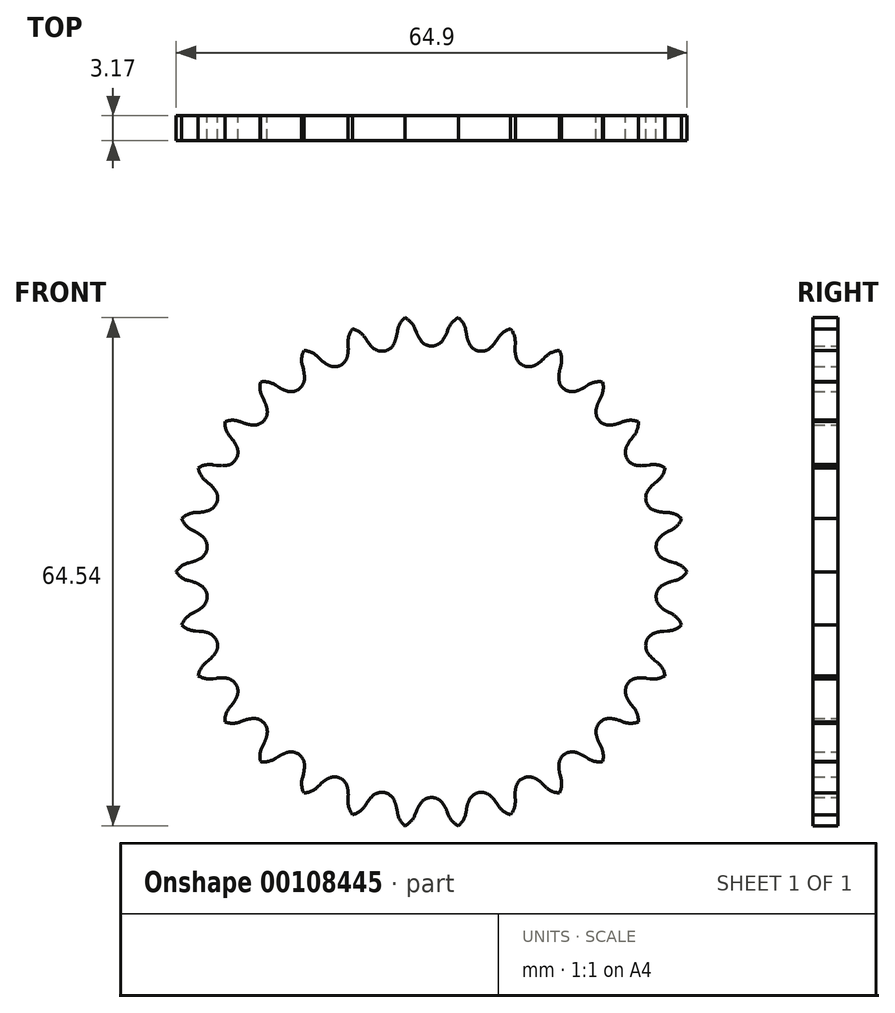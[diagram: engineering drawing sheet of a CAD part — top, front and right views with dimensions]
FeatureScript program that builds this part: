
annotation { "Feature Type Name" : "Feature", "Feature Type Description" : "" }
export const myFeature = defineFeature(function(context is Context, id is Id, definition is map)
    precondition{}
    {
        {
            var Q0;
            Q0=qCreatedBy(makeId("Front.planeOp"),FACE);
            var sketch = newSketch(context, id + "F0", { "sketchPlane" : qUnion([Q0])});
            skCircle(sketch, "E0", {"center": v(0, 0) * mm, "radius": 30.37 * mm, "construction": true});
            skArc(sketch, "E1", {"start": v(-1.36, 29.35) * mm, "mid": v(-0.76, 28.86) * mm, "end": v(0, 28.68) * mm});
            skArc(sketch, "E2", {"start": v(-1.36, 29.35) * mm, "mid": v(-1.69, 29.86) * mm, "end": v(-1.94, 30.42) * mm});
            skLineSegment(sketch, "E3", {"start": v(-1.94, 30.42) * mm, "end": v(-2.1, 30.84) * mm});
            skArc(sketch, "E4.trimOffspring", {"start": v(-2.1, 30.84) * mm, "mid": v(-2.62, 31.68) * mm, "end": v(-3.4, 32.27) * mm});
            skArc(sketch, "E5.MirrorCS", {"start": v(1.36, 29.35) * mm, "mid": v(0.76, 28.86) * mm, "end": v(0, 28.68) * mm});
            skArc(sketch, "E6.MirrorCS", {"start": v(1.36, 29.35) * mm, "mid": v(1.69, 29.86) * mm, "end": v(1.94, 30.42) * mm});
            skLineSegment(sketch, "E7.MirrorCS", {"start": v(1.94, 30.42) * mm, "end": v(2.1, 30.84) * mm});
            skArc(sketch, "E8.MirrorCS", {"start": v(2.1, 30.84) * mm, "mid": v(2.62, 31.68) * mm, "end": v(3.4, 32.27) * mm});
            skArc(sketch, "E9.1.0", {"start": v(-8.47, 29.73) * mm, "mid": v(-9.14, 30.44) * mm, "end": v(-10.03, 30.86) * mm});
            skArc(sketch, "E9.1.1", {"start": v(-7.43, 28.43) * mm, "mid": v(-6.74, 28.07) * mm, "end": v(-5.96, 28.05) * mm});
            skArc(sketch, "E9.1.2", {"start": v(-4.78, 29) * mm, "mid": v(-5.26, 28.38) * mm, "end": v(-5.96, 28.05) * mm});
            skArc(sketch, "E9.1.3", {"start": v(-4.35, 30.6) * mm, "mid": v(-4.03, 31.53) * mm, "end": v(-3.4, 32.27) * mm});
            skArc(sketch, "E9.1.4", {"start": v(-4.78, 29) * mm, "mid": v(-4.56, 29.56) * mm, "end": v(-4.42, 30.16) * mm});
            skLineSegment(sketch, "E9.1.5", {"start": v(-4.42, 30.16) * mm, "end": v(-4.35, 30.6) * mm});
            skArc(sketch, "E9.1.6", {"start": v(-7.43, 28.43) * mm, "mid": v(-7.86, 28.86) * mm, "end": v(-8.22, 29.35) * mm});
            skLineSegment(sketch, "E9.1.7", {"start": v(-8.22, 29.35) * mm, "end": v(-8.47, 29.73) * mm});
            skArc(sketch, "E9.2.0", {"start": v(-14.47, 27.32) * mm, "mid": v(-15.27, 27.87) * mm, "end": v(-16.22, 28.1) * mm});
            skArc(sketch, "E9.2.1", {"start": v(-13.18, 26.26) * mm, "mid": v(-12.43, 26.05) * mm, "end": v(-11.66, 26.2) * mm});
            skArc(sketch, "E9.2.2", {"start": v(-10.7, 27.37) * mm, "mid": v(-11.05, 26.67) * mm, "end": v(-11.66, 26.2) * mm});
            skArc(sketch, "E9.2.3", {"start": v(-10.62, 29.03) * mm, "mid": v(-10.5, 30) * mm, "end": v(-10.03, 30.86) * mm});
            skArc(sketch, "E9.2.4", {"start": v(-10.7, 27.37) * mm, "mid": v(-10.6, 27.97) * mm, "end": v(-10.6, 28.58) * mm});
            skLineSegment(sketch, "E9.2.5", {"start": v(-10.6, 28.58) * mm, "end": v(-10.62, 29.03) * mm});
            skArc(sketch, "E9.2.6", {"start": v(-13.18, 26.26) * mm, "mid": v(-13.69, 26.6) * mm, "end": v(-14.15, 27) * mm});
            skLineSegment(sketch, "E9.2.7", {"start": v(-14.15, 27) * mm, "end": v(-14.47, 27.32) * mm});
            skArc(sketch, "E10.1.3.0", {"start": v(-19.83, 23.71) * mm, "mid": v(-20.74, 24.09) * mm, "end": v(-21.71, 24.11) * mm});
            skArc(sketch, "E10.4.3.0", {"start": v(-18.35, 22.95) * mm, "mid": v(-17.57, 22.9) * mm, "end": v(-16.86, 23.2) * mm});
            skArc(sketch, "E10.8.3.0", {"start": v(-16.16, 24.54) * mm, "mid": v(-16.35, 23.8) * mm, "end": v(-16.86, 23.2) * mm});
            skArc(sketch, "E10.12.3.0", {"start": v(-16.43, 26.2) * mm, "mid": v(-16.5, 27.16) * mm, "end": v(-16.22, 28.1) * mm});
            skArc(sketch, "E10.16.3.0", {"start": v(-16.16, 24.54) * mm, "mid": v(-16.19, 25.15) * mm, "end": v(-16.3, 25.75) * mm});
            skLineSegment(sketch, "E10.20.3.0", {"start": v(-16.3, 25.75) * mm, "end": v(-16.43, 26.2) * mm});
            skArc(sketch, "E10.23.3.0", {"start": v(-18.35, 22.95) * mm, "mid": v(-18.92, 23.17) * mm, "end": v(-19.45, 23.47) * mm});
            skLineSegment(sketch, "E10.27.3.0", {"start": v(-19.45, 23.47) * mm, "end": v(-19.83, 23.71) * mm});
            skArc(sketch, "E10.1.4.0", {"start": v(-24.33, 19.07) * mm, "mid": v(-25.3, 19.25) * mm, "end": v(-26.25, 19.07) * mm});
            skArc(sketch, "E10.4.4.0", {"start": v(-22.72, 18.63) * mm, "mid": v(-21.95, 18.75) * mm, "end": v(-21.31, 19.19) * mm});
            skArc(sketch, "E10.8.4.0", {"start": v(-20.9, 20.65) * mm, "mid": v(-20.94, 19.87) * mm, "end": v(-21.31, 19.19) * mm});
            skArc(sketch, "E10.12.4.0", {"start": v(-21.51, 22.2) * mm, "mid": v(-21.8, 23.14) * mm, "end": v(-21.71, 24.11) * mm});
            skArc(sketch, "E10.16.4.0", {"start": v(-20.9, 20.65) * mm, "mid": v(-21.07, 21.24) * mm, "end": v(-21.3, 21.8) * mm});
            skLineSegment(sketch, "E10.20.4.0", {"start": v(-21.3, 21.8) * mm, "end": v(-21.51, 22.2) * mm});
            skArc(sketch, "E10.23.4.0", {"start": v(-22.72, 18.63) * mm, "mid": v(-23.32, 18.73) * mm, "end": v(-23.9, 18.9) * mm});
            skLineSegment(sketch, "E10.27.4.0", {"start": v(-23.9, 18.9) * mm, "end": v(-24.33, 19.07) * mm});
            skArc(sketch, "E10.1.5.0", {"start": v(-27.76, 13.6) * mm, "mid": v(-28.74, 13.57) * mm, "end": v(-29.64, 13.2) * mm});
            skArc(sketch, "E10.4.5.0", {"start": v(-26.1, 13.5) * mm, "mid": v(-25.37, 13.77) * mm, "end": v(-24.84, 14.34) * mm});
            skArc(sketch, "E10.8.5.0", {"start": v(-24.74, 15.85) * mm, "mid": v(-24.61, 15.08) * mm, "end": v(-24.84, 14.34) * mm});
            skArc(sketch, "E10.12.5.0", {"start": v(-25.66, 17.25) * mm, "mid": v(-26.12, 18.1) * mm, "end": v(-26.25, 19.07) * mm});
            skArc(sketch, "E10.16.5.0", {"start": v(-24.74, 15.85) * mm, "mid": v(-25.02, 16.4) * mm, "end": v(-25.37, 16.9) * mm});
            skLineSegment(sketch, "E10.20.5.0", {"start": v(-25.37, 16.9) * mm, "end": v(-25.66, 17.25) * mm});
            skArc(sketch, "E10.23.5.0", {"start": v(-26.1, 13.5) * mm, "mid": v(-26.7, 13.47) * mm, "end": v(-27.31, 13.53) * mm});
            skLineSegment(sketch, "E10.27.5.0", {"start": v(-27.31, 13.53) * mm, "end": v(-27.76, 13.6) * mm});
            skArc(sketch, "E10.1.6.0", {"start": v(-29.98, 7.53) * mm, "mid": v(-30.93, 7.3) * mm, "end": v(-31.74, 6.75) * mm});
            skArc(sketch, "E10.4.6.0", {"start": v(-28.34, 7.78) * mm, "mid": v(-27.68, 8.2) * mm, "end": v(-27.27, 8.86) * mm});
            skArc(sketch, "E10.8.6.0", {"start": v(-27.5, 10.36) * mm, "mid": v(-27.2, 9.64) * mm, "end": v(-27.27, 8.86) * mm});
            skArc(sketch, "E10.12.6.0", {"start": v(-28.68, 11.53) * mm, "mid": v(-29.32, 12.28) * mm, "end": v(-29.64, 13.2) * mm});
            skArc(sketch, "E10.16.6.0", {"start": v(-27.5, 10.36) * mm, "mid": v(-27.88, 10.83) * mm, "end": v(-28.33, 11.25) * mm});
            skLineSegment(sketch, "E10.20.6.0", {"start": v(-28.33, 11.25) * mm, "end": v(-28.68, 11.53) * mm});
            skArc(sketch, "E10.23.6.0", {"start": v(-28.34, 7.78) * mm, "mid": v(-28.92, 7.62) * mm, "end": v(-29.53, 7.55) * mm});
            skLineSegment(sketch, "E10.27.6.0", {"start": v(-29.53, 7.55) * mm, "end": v(-29.98, 7.53) * mm});
            skArc(sketch, "E10.1.7.0", {"start": v(-30.9, 1.13) * mm, "mid": v(-31.78, 0.7) * mm, "end": v(-32.45, 0) * mm});
            skArc(sketch, "E10.4.7.0", {"start": v(-29.33, 1.72) * mm, "mid": v(-28.78, 2.26) * mm, "end": v(-28.52, 3) * mm});
            skArc(sketch, "E10.8.7.0", {"start": v(-29.05, 4.42) * mm, "mid": v(-28.62, 3.77) * mm, "end": v(-28.52, 3) * mm});
            skArc(sketch, "E10.12.7.0", {"start": v(-30.45, 5.32) * mm, "mid": v(-31.23, 5.91) * mm, "end": v(-31.74, 6.75) * mm});
            skArc(sketch, "E10.16.7.0", {"start": v(-29.05, 4.42) * mm, "mid": v(-29.52, 4.8) * mm, "end": v(-30.05, 5.11) * mm});
            skLineSegment(sketch, "E10.20.7.0", {"start": v(-30.05, 5.11) * mm, "end": v(-30.45, 5.32) * mm});
            skArc(sketch, "E10.23.7.0", {"start": v(-29.33, 1.72) * mm, "mid": v(-29.88, 1.44) * mm, "end": v(-30.45, 1.25) * mm});
            skLineSegment(sketch, "E10.27.7.0", {"start": v(-30.45, 1.25) * mm, "end": v(-30.9, 1.13) * mm});
            skArc(sketch, "E10.1.8.0", {"start": v(-30.45, -5.32) * mm, "mid": v(-31.23, -5.91) * mm, "end": v(-31.74, -6.75) * mm});
            skArc(sketch, "E10.4.8.0", {"start": v(-29.05, -4.42) * mm, "mid": v(-28.62, -3.77) * mm, "end": v(-28.52, -3) * mm});
            skArc(sketch, "E10.8.8.0", {"start": v(-29.33, -1.72) * mm, "mid": v(-28.78, -2.26) * mm, "end": v(-28.52, -3) * mm});
            skArc(sketch, "E10.12.8.0", {"start": v(-30.9, -1.13) * mm, "mid": v(-31.78, -0.7) * mm, "end": v(-32.45, 0) * mm});
            skArc(sketch, "E10.16.8.0", {"start": v(-29.33, -1.72) * mm, "mid": v(-29.88, -1.44) * mm, "end": v(-30.45, -1.25) * mm});
            skLineSegment(sketch, "E10.20.8.0", {"start": v(-30.45, -1.25) * mm, "end": v(-30.9, -1.13) * mm});
            skArc(sketch, "E10.23.8.0", {"start": v(-29.05, -4.42) * mm, "mid": v(-29.52, -4.8) * mm, "end": v(-30.05, -5.11) * mm});
            skLineSegment(sketch, "E10.27.8.0", {"start": v(-30.05, -5.11) * mm, "end": v(-30.45, -5.32) * mm});
            skArc(sketch, "E10.1.9.0", {"start": v(-28.68, -11.53) * mm, "mid": v(-29.32, -12.28) * mm, "end": v(-29.64, -13.2) * mm});
            skArc(sketch, "E10.4.9.0", {"start": v(-27.5, -10.36) * mm, "mid": v(-27.2, -9.64) * mm, "end": v(-27.27, -8.86) * mm});
            skArc(sketch, "E10.8.9.0", {"start": v(-28.34, -7.78) * mm, "mid": v(-27.68, -8.2) * mm, "end": v(-27.27, -8.86) * mm});
            skArc(sketch, "E10.12.9.0", {"start": v(-29.98, -7.53) * mm, "mid": v(-30.93, -7.3) * mm, "end": v(-31.74, -6.75) * mm});
            skArc(sketch, "E10.16.9.0", {"start": v(-28.34, -7.78) * mm, "mid": v(-28.92, -7.62) * mm, "end": v(-29.53, -7.55) * mm});
            skLineSegment(sketch, "E10.20.9.0", {"start": v(-29.53, -7.55) * mm, "end": v(-29.98, -7.53) * mm});
            skArc(sketch, "E10.23.9.0", {"start": v(-27.5, -10.36) * mm, "mid": v(-27.88, -10.83) * mm, "end": v(-28.33, -11.25) * mm});
            skLineSegment(sketch, "E10.27.9.0", {"start": v(-28.33, -11.25) * mm, "end": v(-28.68, -11.53) * mm});
            skArc(sketch, "E10.1.10.0", {"start": v(-25.66, -17.25) * mm, "mid": v(-26.12, -18.1) * mm, "end": v(-26.25, -19.07) * mm});
            skArc(sketch, "E10.4.10.0", {"start": v(-24.74, -15.85) * mm, "mid": v(-24.61, -15.08) * mm, "end": v(-24.84, -14.34) * mm});
            skArc(sketch, "E10.8.10.0", {"start": v(-26.1, -13.5) * mm, "mid": v(-25.37, -13.77) * mm, "end": v(-24.84, -14.34) * mm});
            skArc(sketch, "E10.12.10.0", {"start": v(-27.76, -13.6) * mm, "mid": v(-28.74, -13.57) * mm, "end": v(-29.64, -13.2) * mm});
            skArc(sketch, "E10.16.10.0", {"start": v(-26.1, -13.5) * mm, "mid": v(-26.7, -13.47) * mm, "end": v(-27.31, -13.53) * mm});
            skLineSegment(sketch, "E10.20.10.0", {"start": v(-27.31, -13.53) * mm, "end": v(-27.76, -13.6) * mm});
            skArc(sketch, "E10.23.10.0", {"start": v(-24.74, -15.85) * mm, "mid": v(-25.02, -16.4) * mm, "end": v(-25.37, -16.9) * mm});
            skLineSegment(sketch, "E10.27.10.0", {"start": v(-25.37, -16.9) * mm, "end": v(-25.66, -17.25) * mm});
            skArc(sketch, "E10.1.11.0", {"start": v(-21.51, -22.2) * mm, "mid": v(-21.8, -23.14) * mm, "end": v(-21.71, -24.11) * mm});
            skArc(sketch, "E10.4.11.0", {"start": v(-20.9, -20.65) * mm, "mid": v(-20.94, -19.87) * mm, "end": v(-21.31, -19.19) * mm});
            skArc(sketch, "E10.8.11.0", {"start": v(-22.72, -18.63) * mm, "mid": v(-21.95, -18.75) * mm, "end": v(-21.31, -19.19) * mm});
            skArc(sketch, "E10.12.11.0", {"start": v(-24.33, -19.07) * mm, "mid": v(-25.3, -19.25) * mm, "end": v(-26.25, -19.07) * mm});
            skArc(sketch, "E10.16.11.0", {"start": v(-22.72, -18.63) * mm, "mid": v(-23.32, -18.73) * mm, "end": v(-23.9, -18.9) * mm});
            skLineSegment(sketch, "E10.20.11.0", {"start": v(-23.9, -18.9) * mm, "end": v(-24.33, -19.07) * mm});
            skArc(sketch, "E10.23.11.0", {"start": v(-20.9, -20.65) * mm, "mid": v(-21.07, -21.24) * mm, "end": v(-21.3, -21.8) * mm});
            skLineSegment(sketch, "E10.27.11.0", {"start": v(-21.3, -21.8) * mm, "end": v(-21.51, -22.2) * mm});
            skArc(sketch, "E10.1.12.0", {"start": v(-16.43, -26.2) * mm, "mid": v(-16.5, -27.16) * mm, "end": v(-16.22, -28.1) * mm});
            skArc(sketch, "E10.4.12.0", {"start": v(-16.16, -24.54) * mm, "mid": v(-16.35, -23.8) * mm, "end": v(-16.86, -23.2) * mm});
            skArc(sketch, "E10.8.12.0", {"start": v(-18.35, -22.95) * mm, "mid": v(-17.57, -22.9) * mm, "end": v(-16.86, -23.2) * mm});
            skArc(sketch, "E10.12.12.0", {"start": v(-19.83, -23.71) * mm, "mid": v(-20.74, -24.09) * mm, "end": v(-21.71, -24.11) * mm});
            skArc(sketch, "E10.16.12.0", {"start": v(-18.35, -22.95) * mm, "mid": v(-18.92, -23.17) * mm, "end": v(-19.45, -23.47) * mm});
            skLineSegment(sketch, "E10.20.12.0", {"start": v(-19.45, -23.47) * mm, "end": v(-19.83, -23.71) * mm});
            skArc(sketch, "E10.23.12.0", {"start": v(-16.16, -24.54) * mm, "mid": v(-16.19, -25.15) * mm, "end": v(-16.3, -25.75) * mm});
            skLineSegment(sketch, "E10.27.12.0", {"start": v(-16.3, -25.75) * mm, "end": v(-16.43, -26.2) * mm});
            skArc(sketch, "E10.1.13.0", {"start": v(-10.62, -29.03) * mm, "mid": v(-10.5, -30) * mm, "end": v(-10.03, -30.86) * mm});
            skArc(sketch, "E10.4.13.0", {"start": v(-10.7, -27.37) * mm, "mid": v(-11.05, -26.67) * mm, "end": v(-11.66, -26.2) * mm});
            skArc(sketch, "E10.8.13.0", {"start": v(-13.18, -26.26) * mm, "mid": v(-12.43, -26.05) * mm, "end": v(-11.66, -26.2) * mm});
            skArc(sketch, "E10.12.13.0", {"start": v(-14.47, -27.32) * mm, "mid": v(-15.27, -27.87) * mm, "end": v(-16.22, -28.1) * mm});
            skArc(sketch, "E10.16.13.0", {"start": v(-13.18, -26.26) * mm, "mid": v(-13.69, -26.6) * mm, "end": v(-14.15, -27) * mm});
            skLineSegment(sketch, "E10.20.13.0", {"start": v(-14.15, -27) * mm, "end": v(-14.47, -27.32) * mm});
            skArc(sketch, "E10.23.13.0", {"start": v(-10.7, -27.37) * mm, "mid": v(-10.6, -27.97) * mm, "end": v(-10.6, -28.58) * mm});
            skLineSegment(sketch, "E10.27.13.0", {"start": v(-10.6, -28.58) * mm, "end": v(-10.62, -29.03) * mm});
            skArc(sketch, "E10.1.14.0", {"start": v(-4.35, -30.6) * mm, "mid": v(-4.03, -31.53) * mm, "end": v(-3.4, -32.27) * mm});
            skArc(sketch, "E10.4.14.0", {"start": v(-4.78, -29) * mm, "mid": v(-5.26, -28.38) * mm, "end": v(-5.96, -28.05) * mm});
            skArc(sketch, "E10.8.14.0", {"start": v(-7.43, -28.43) * mm, "mid": v(-6.74, -28.07) * mm, "end": v(-5.96, -28.05) * mm});
            skArc(sketch, "E10.12.14.0", {"start": v(-8.47, -29.73) * mm, "mid": v(-9.14, -30.44) * mm, "end": v(-10.03, -30.86) * mm});
            skArc(sketch, "E10.16.14.0", {"start": v(-7.43, -28.43) * mm, "mid": v(-7.86, -28.86) * mm, "end": v(-8.22, -29.35) * mm});
            skLineSegment(sketch, "E10.20.14.0", {"start": v(-8.22, -29.35) * mm, "end": v(-8.47, -29.73) * mm});
            skArc(sketch, "E10.23.14.0", {"start": v(-4.78, -29) * mm, "mid": v(-4.56, -29.56) * mm, "end": v(-4.42, -30.16) * mm});
            skLineSegment(sketch, "E10.27.14.0", {"start": v(-4.42, -30.16) * mm, "end": v(-4.35, -30.6) * mm});
            skArc(sketch, "E10.1.15.0", {"start": v(2.1, -30.84) * mm, "mid": v(2.62, -31.68) * mm, "end": v(3.4, -32.27) * mm});
            skArc(sketch, "E10.4.15.0", {"start": v(1.36, -29.35) * mm, "mid": v(0.76, -28.86) * mm, "end": v(0, -28.68) * mm});
            skArc(sketch, "E10.8.15.0", {"start": v(-1.36, -29.35) * mm, "mid": v(-0.76, -28.86) * mm, "end": v(0, -28.68) * mm});
            skArc(sketch, "E10.12.15.0", {"start": v(-2.1, -30.84) * mm, "mid": v(-2.62, -31.68) * mm, "end": v(-3.4, -32.27) * mm});
            skArc(sketch, "E10.16.15.0", {"start": v(-1.36, -29.35) * mm, "mid": v(-1.69, -29.86) * mm, "end": v(-1.94, -30.42) * mm});
            skLineSegment(sketch, "E10.20.15.0", {"start": v(-1.94, -30.42) * mm, "end": v(-2.1, -30.84) * mm});
            skArc(sketch, "E10.23.15.0", {"start": v(1.36, -29.35) * mm, "mid": v(1.69, -29.86) * mm, "end": v(1.94, -30.42) * mm});
            skLineSegment(sketch, "E10.27.15.0", {"start": v(1.94, -30.42) * mm, "end": v(2.1, -30.84) * mm});
            skArc(sketch, "E10.1.16.0", {"start": v(8.47, -29.73) * mm, "mid": v(9.14, -30.44) * mm, "end": v(10.03, -30.86) * mm});
            skArc(sketch, "E10.4.16.0", {"start": v(7.43, -28.43) * mm, "mid": v(6.74, -28.07) * mm, "end": v(5.96, -28.05) * mm});
            skArc(sketch, "E10.8.16.0", {"start": v(4.78, -29) * mm, "mid": v(5.26, -28.38) * mm, "end": v(5.96, -28.05) * mm});
            skArc(sketch, "E10.12.16.0", {"start": v(4.35, -30.6) * mm, "mid": v(4.03, -31.53) * mm, "end": v(3.4, -32.27) * mm});
            skArc(sketch, "E10.16.16.0", {"start": v(4.78, -29) * mm, "mid": v(4.56, -29.56) * mm, "end": v(4.42, -30.16) * mm});
            skLineSegment(sketch, "E10.20.16.0", {"start": v(4.42, -30.16) * mm, "end": v(4.35, -30.6) * mm});
            skArc(sketch, "E10.23.16.0", {"start": v(7.43, -28.43) * mm, "mid": v(7.86, -28.86) * mm, "end": v(8.22, -29.35) * mm});
            skLineSegment(sketch, "E10.27.16.0", {"start": v(8.22, -29.35) * mm, "end": v(8.47, -29.73) * mm});
            skArc(sketch, "E10.1.17.0", {"start": v(14.47, -27.32) * mm, "mid": v(15.27, -27.87) * mm, "end": v(16.22, -28.1) * mm});
            skArc(sketch, "E10.4.17.0", {"start": v(13.18, -26.26) * mm, "mid": v(12.43, -26.05) * mm, "end": v(11.66, -26.2) * mm});
            skArc(sketch, "E10.8.17.0", {"start": v(10.7, -27.37) * mm, "mid": v(11.05, -26.67) * mm, "end": v(11.66, -26.2) * mm});
            skArc(sketch, "E10.12.17.0", {"start": v(10.62, -29.03) * mm, "mid": v(10.5, -30) * mm, "end": v(10.03, -30.86) * mm});
            skArc(sketch, "E10.16.17.0", {"start": v(10.7, -27.37) * mm, "mid": v(10.6, -27.97) * mm, "end": v(10.6, -28.58) * mm});
            skLineSegment(sketch, "E10.20.17.0", {"start": v(10.6, -28.58) * mm, "end": v(10.62, -29.03) * mm});
            skArc(sketch, "E10.23.17.0", {"start": v(13.18, -26.26) * mm, "mid": v(13.69, -26.6) * mm, "end": v(14.15, -27) * mm});
            skLineSegment(sketch, "E10.27.17.0", {"start": v(14.15, -27) * mm, "end": v(14.47, -27.32) * mm});
            skArc(sketch, "E10.1.18.0", {"start": v(19.83, -23.71) * mm, "mid": v(20.74, -24.09) * mm, "end": v(21.71, -24.11) * mm});
            skArc(sketch, "E10.4.18.0", {"start": v(18.35, -22.95) * mm, "mid": v(17.57, -22.9) * mm, "end": v(16.86, -23.2) * mm});
            skArc(sketch, "E10.8.18.0", {"start": v(16.16, -24.54) * mm, "mid": v(16.35, -23.8) * mm, "end": v(16.86, -23.2) * mm});
            skArc(sketch, "E10.12.18.0", {"start": v(16.43, -26.2) * mm, "mid": v(16.5, -27.16) * mm, "end": v(16.22, -28.1) * mm});
            skArc(sketch, "E10.16.18.0", {"start": v(16.16, -24.54) * mm, "mid": v(16.19, -25.15) * mm, "end": v(16.3, -25.75) * mm});
            skLineSegment(sketch, "E10.20.18.0", {"start": v(16.3, -25.75) * mm, "end": v(16.43, -26.2) * mm});
            skArc(sketch, "E10.23.18.0", {"start": v(18.35, -22.95) * mm, "mid": v(18.92, -23.17) * mm, "end": v(19.45, -23.47) * mm});
            skLineSegment(sketch, "E10.27.18.0", {"start": v(19.45, -23.47) * mm, "end": v(19.83, -23.71) * mm});
            skArc(sketch, "E10.1.19.0", {"start": v(24.33, -19.07) * mm, "mid": v(25.3, -19.25) * mm, "end": v(26.25, -19.07) * mm});
            skArc(sketch, "E10.4.19.0", {"start": v(22.72, -18.63) * mm, "mid": v(21.95, -18.75) * mm, "end": v(21.31, -19.19) * mm});
            skArc(sketch, "E10.8.19.0", {"start": v(20.9, -20.65) * mm, "mid": v(20.94, -19.87) * mm, "end": v(21.31, -19.19) * mm});
            skArc(sketch, "E10.12.19.0", {"start": v(21.51, -22.2) * mm, "mid": v(21.8, -23.14) * mm, "end": v(21.71, -24.11) * mm});
            skArc(sketch, "E10.16.19.0", {"start": v(20.9, -20.65) * mm, "mid": v(21.07, -21.24) * mm, "end": v(21.3, -21.8) * mm});
            skLineSegment(sketch, "E10.20.19.0", {"start": v(21.3, -21.8) * mm, "end": v(21.51, -22.2) * mm});
            skArc(sketch, "E10.23.19.0", {"start": v(22.72, -18.63) * mm, "mid": v(23.32, -18.73) * mm, "end": v(23.9, -18.9) * mm});
            skLineSegment(sketch, "E10.27.19.0", {"start": v(23.9, -18.9) * mm, "end": v(24.33, -19.07) * mm});
            skArc(sketch, "E10.1.20.0", {"start": v(27.76, -13.6) * mm, "mid": v(28.74, -13.57) * mm, "end": v(29.64, -13.2) * mm});
            skArc(sketch, "E10.4.20.0", {"start": v(26.1, -13.5) * mm, "mid": v(25.37, -13.77) * mm, "end": v(24.84, -14.34) * mm});
            skArc(sketch, "E10.8.20.0", {"start": v(24.74, -15.85) * mm, "mid": v(24.61, -15.08) * mm, "end": v(24.84, -14.34) * mm});
            skArc(sketch, "E10.12.20.0", {"start": v(25.66, -17.25) * mm, "mid": v(26.12, -18.1) * mm, "end": v(26.25, -19.07) * mm});
            skArc(sketch, "E10.16.20.0", {"start": v(24.74, -15.85) * mm, "mid": v(25.02, -16.4) * mm, "end": v(25.37, -16.9) * mm});
            skLineSegment(sketch, "E10.20.20.0", {"start": v(25.37, -16.9) * mm, "end": v(25.66, -17.25) * mm});
            skArc(sketch, "E10.23.20.0", {"start": v(26.1, -13.5) * mm, "mid": v(26.7, -13.47) * mm, "end": v(27.31, -13.53) * mm});
            skLineSegment(sketch, "E10.27.20.0", {"start": v(27.31, -13.53) * mm, "end": v(27.76, -13.6) * mm});
            skArc(sketch, "E10.1.21.0", {"start": v(29.98, -7.53) * mm, "mid": v(30.93, -7.3) * mm, "end": v(31.74, -6.75) * mm});
            skArc(sketch, "E10.4.21.0", {"start": v(28.34, -7.78) * mm, "mid": v(27.68, -8.2) * mm, "end": v(27.27, -8.86) * mm});
            skArc(sketch, "E10.8.21.0", {"start": v(27.5, -10.36) * mm, "mid": v(27.2, -9.64) * mm, "end": v(27.27, -8.86) * mm});
            skArc(sketch, "E10.12.21.0", {"start": v(28.68, -11.53) * mm, "mid": v(29.32, -12.28) * mm, "end": v(29.64, -13.2) * mm});
            skArc(sketch, "E10.16.21.0", {"start": v(27.5, -10.36) * mm, "mid": v(27.88, -10.83) * mm, "end": v(28.33, -11.25) * mm});
            skLineSegment(sketch, "E10.20.21.0", {"start": v(28.33, -11.25) * mm, "end": v(28.68, -11.53) * mm});
            skArc(sketch, "E10.23.21.0", {"start": v(28.34, -7.78) * mm, "mid": v(28.92, -7.62) * mm, "end": v(29.53, -7.55) * mm});
            skLineSegment(sketch, "E10.27.21.0", {"start": v(29.53, -7.55) * mm, "end": v(29.98, -7.53) * mm});
            skArc(sketch, "E10.1.22.0", {"start": v(30.9, -1.13) * mm, "mid": v(31.78, -0.7) * mm, "end": v(32.45, 0) * mm});
            skArc(sketch, "E10.4.22.0", {"start": v(29.33, -1.72) * mm, "mid": v(28.78, -2.26) * mm, "end": v(28.52, -3) * mm});
            skArc(sketch, "E10.8.22.0", {"start": v(29.05, -4.42) * mm, "mid": v(28.62, -3.77) * mm, "end": v(28.52, -3) * mm});
            skArc(sketch, "E10.12.22.0", {"start": v(30.45, -5.32) * mm, "mid": v(31.23, -5.91) * mm, "end": v(31.74, -6.75) * mm});
            skArc(sketch, "E10.16.22.0", {"start": v(29.05, -4.42) * mm, "mid": v(29.52, -4.8) * mm, "end": v(30.05, -5.11) * mm});
            skLineSegment(sketch, "E10.20.22.0", {"start": v(30.05, -5.11) * mm, "end": v(30.45, -5.32) * mm});
            skArc(sketch, "E10.23.22.0", {"start": v(29.33, -1.72) * mm, "mid": v(29.88, -1.44) * mm, "end": v(30.45, -1.25) * mm});
            skLineSegment(sketch, "E10.27.22.0", {"start": v(30.45, -1.25) * mm, "end": v(30.9, -1.13) * mm});
            skArc(sketch, "E10.1.23.0", {"start": v(30.45, 5.32) * mm, "mid": v(31.23, 5.91) * mm, "end": v(31.74, 6.75) * mm});
            skArc(sketch, "E10.4.23.0", {"start": v(29.05, 4.42) * mm, "mid": v(28.62, 3.77) * mm, "end": v(28.52, 3) * mm});
            skArc(sketch, "E10.8.23.0", {"start": v(29.33, 1.72) * mm, "mid": v(28.78, 2.26) * mm, "end": v(28.52, 3) * mm});
            skArc(sketch, "E10.12.23.0", {"start": v(30.9, 1.13) * mm, "mid": v(31.78, 0.7) * mm, "end": v(32.45, 0) * mm});
            skArc(sketch, "E10.16.23.0", {"start": v(29.33, 1.72) * mm, "mid": v(29.88, 1.44) * mm, "end": v(30.45, 1.25) * mm});
            skLineSegment(sketch, "E10.20.23.0", {"start": v(30.45, 1.25) * mm, "end": v(30.9, 1.13) * mm});
            skArc(sketch, "E10.23.23.0", {"start": v(29.05, 4.42) * mm, "mid": v(29.52, 4.8) * mm, "end": v(30.05, 5.11) * mm});
            skLineSegment(sketch, "E10.27.23.0", {"start": v(30.05, 5.11) * mm, "end": v(30.45, 5.32) * mm});
            skArc(sketch, "E10.1.24.0", {"start": v(28.68, 11.53) * mm, "mid": v(29.32, 12.28) * mm, "end": v(29.64, 13.2) * mm});
            skArc(sketch, "E10.4.24.0", {"start": v(27.5, 10.36) * mm, "mid": v(27.2, 9.64) * mm, "end": v(27.27, 8.86) * mm});
            skArc(sketch, "E10.8.24.0", {"start": v(28.34, 7.78) * mm, "mid": v(27.68, 8.2) * mm, "end": v(27.27, 8.86) * mm});
            skArc(sketch, "E10.12.24.0", {"start": v(29.98, 7.53) * mm, "mid": v(30.93, 7.3) * mm, "end": v(31.74, 6.75) * mm});
            skArc(sketch, "E10.16.24.0", {"start": v(28.34, 7.78) * mm, "mid": v(28.92, 7.62) * mm, "end": v(29.53, 7.55) * mm});
            skLineSegment(sketch, "E10.20.24.0", {"start": v(29.53, 7.55) * mm, "end": v(29.98, 7.53) * mm});
            skArc(sketch, "E10.23.24.0", {"start": v(27.5, 10.36) * mm, "mid": v(27.88, 10.83) * mm, "end": v(28.33, 11.25) * mm});
            skLineSegment(sketch, "E10.27.24.0", {"start": v(28.33, 11.25) * mm, "end": v(28.68, 11.53) * mm});
            skArc(sketch, "E10.1.25.0", {"start": v(25.66, 17.25) * mm, "mid": v(26.12, 18.1) * mm, "end": v(26.25, 19.07) * mm});
            skArc(sketch, "E10.4.25.0", {"start": v(24.74, 15.85) * mm, "mid": v(24.61, 15.08) * mm, "end": v(24.84, 14.34) * mm});
            skArc(sketch, "E10.8.25.0", {"start": v(26.1, 13.5) * mm, "mid": v(25.37, 13.77) * mm, "end": v(24.84, 14.34) * mm});
            skArc(sketch, "E10.12.25.0", {"start": v(27.76, 13.6) * mm, "mid": v(28.74, 13.57) * mm, "end": v(29.64, 13.2) * mm});
            skArc(sketch, "E10.16.25.0", {"start": v(26.1, 13.5) * mm, "mid": v(26.7, 13.47) * mm, "end": v(27.31, 13.53) * mm});
            skLineSegment(sketch, "E10.20.25.0", {"start": v(27.31, 13.53) * mm, "end": v(27.76, 13.6) * mm});
            skArc(sketch, "E10.23.25.0", {"start": v(24.74, 15.85) * mm, "mid": v(25.02, 16.4) * mm, "end": v(25.37, 16.9) * mm});
            skLineSegment(sketch, "E10.27.25.0", {"start": v(25.37, 16.9) * mm, "end": v(25.66, 17.25) * mm});
            skArc(sketch, "E10.1.26.0", {"start": v(21.51, 22.2) * mm, "mid": v(21.8, 23.14) * mm, "end": v(21.71, 24.11) * mm});
            skArc(sketch, "E10.4.26.0", {"start": v(20.9, 20.65) * mm, "mid": v(20.94, 19.87) * mm, "end": v(21.31, 19.19) * mm});
            skArc(sketch, "E10.8.26.0", {"start": v(22.72, 18.63) * mm, "mid": v(21.95, 18.75) * mm, "end": v(21.31, 19.19) * mm});
            skArc(sketch, "E10.12.26.0", {"start": v(24.33, 19.07) * mm, "mid": v(25.3, 19.25) * mm, "end": v(26.25, 19.07) * mm});
            skArc(sketch, "E10.16.26.0", {"start": v(22.72, 18.63) * mm, "mid": v(23.32, 18.73) * mm, "end": v(23.9, 18.9) * mm});
            skLineSegment(sketch, "E10.20.26.0", {"start": v(23.9, 18.9) * mm, "end": v(24.33, 19.07) * mm});
            skArc(sketch, "E10.23.26.0", {"start": v(20.9, 20.65) * mm, "mid": v(21.07, 21.24) * mm, "end": v(21.3, 21.8) * mm});
            skLineSegment(sketch, "E10.27.26.0", {"start": v(21.3, 21.8) * mm, "end": v(21.51, 22.2) * mm});
            skArc(sketch, "E10.1.27.0", {"start": v(16.43, 26.2) * mm, "mid": v(16.5, 27.16) * mm, "end": v(16.22, 28.1) * mm});
            skArc(sketch, "E10.4.27.0", {"start": v(16.16, 24.54) * mm, "mid": v(16.35, 23.8) * mm, "end": v(16.86, 23.2) * mm});
            skArc(sketch, "E10.8.27.0", {"start": v(18.35, 22.95) * mm, "mid": v(17.57, 22.9) * mm, "end": v(16.86, 23.2) * mm});
            skArc(sketch, "E10.12.27.0", {"start": v(19.83, 23.71) * mm, "mid": v(20.74, 24.09) * mm, "end": v(21.71, 24.11) * mm});
            skArc(sketch, "E10.16.27.0", {"start": v(18.35, 22.95) * mm, "mid": v(18.92, 23.17) * mm, "end": v(19.45, 23.47) * mm});
            skLineSegment(sketch, "E10.20.27.0", {"start": v(19.45, 23.47) * mm, "end": v(19.83, 23.71) * mm});
            skArc(sketch, "E10.23.27.0", {"start": v(16.16, 24.54) * mm, "mid": v(16.19, 25.15) * mm, "end": v(16.3, 25.75) * mm});
            skLineSegment(sketch, "E10.27.27.0", {"start": v(16.3, 25.75) * mm, "end": v(16.43, 26.2) * mm});
            skArc(sketch, "E10.1.28.0", {"start": v(10.62, 29.03) * mm, "mid": v(10.5, 30) * mm, "end": v(10.03, 30.86) * mm});
            skArc(sketch, "E10.4.28.0", {"start": v(10.7, 27.37) * mm, "mid": v(11.05, 26.67) * mm, "end": v(11.66, 26.2) * mm});
            skArc(sketch, "E10.8.28.0", {"start": v(13.18, 26.26) * mm, "mid": v(12.43, 26.05) * mm, "end": v(11.66, 26.2) * mm});
            skArc(sketch, "E10.12.28.0", {"start": v(14.47, 27.32) * mm, "mid": v(15.27, 27.87) * mm, "end": v(16.22, 28.1) * mm});
            skArc(sketch, "E10.16.28.0", {"start": v(13.18, 26.26) * mm, "mid": v(13.69, 26.6) * mm, "end": v(14.15, 27) * mm});
            skLineSegment(sketch, "E10.20.28.0", {"start": v(14.15, 27) * mm, "end": v(14.47, 27.32) * mm});
            skArc(sketch, "E10.23.28.0", {"start": v(10.7, 27.37) * mm, "mid": v(10.6, 27.97) * mm, "end": v(10.6, 28.58) * mm});
            skLineSegment(sketch, "E10.27.28.0", {"start": v(10.6, 28.58) * mm, "end": v(10.62, 29.03) * mm});
            skArc(sketch, "E10.1.29.0", {"start": v(4.35, 30.6) * mm, "mid": v(4.03, 31.53) * mm, "end": v(3.4, 32.27) * mm});
            skArc(sketch, "E10.4.29.0", {"start": v(4.78, 29) * mm, "mid": v(5.26, 28.38) * mm, "end": v(5.96, 28.05) * mm});
            skArc(sketch, "E10.8.29.0", {"start": v(7.43, 28.43) * mm, "mid": v(6.74, 28.07) * mm, "end": v(5.96, 28.05) * mm});
            skArc(sketch, "E10.12.29.0", {"start": v(8.47, 29.73) * mm, "mid": v(9.14, 30.44) * mm, "end": v(10.03, 30.86) * mm});
            skArc(sketch, "E10.16.29.0", {"start": v(7.43, 28.43) * mm, "mid": v(7.86, 28.86) * mm, "end": v(8.22, 29.35) * mm});
            skLineSegment(sketch, "E10.20.29.0", {"start": v(8.22, 29.35) * mm, "end": v(8.47, 29.73) * mm});
            skArc(sketch, "E10.23.29.0", {"start": v(4.78, 29) * mm, "mid": v(4.56, 29.56) * mm, "end": v(4.42, 30.16) * mm});
            skLineSegment(sketch, "E10.27.29.0", {"start": v(4.42, 30.16) * mm, "end": v(4.35, 30.6) * mm});
            skSolve(sketch);
        }
        {
            var Q0;
            Q0=makeQuery(id+"F0.imprint","IMPRINT",FACE,{"disambiguationData":[TD([[makeQuery(id+"F0.imprint","IMPRINT",EDGE,{"derivedFrom":sQuery(id+"F0.wireOp",EDGE,"E1")}),-1.0]])]});
            var Q1;
            Q1=makeQuery(id+"F0.imprint","IMPRINT",FACE,{"disambiguationData":[TD([[makeQuery(id+"F0.imprint","IMPRINT",EDGE,{"derivedFrom":sQuery(id+"F0.wireOp",EDGE,"E1")}),1.0]])]});
            extrude(context, id + "F1", {"entities" : qUnion([Q0, Q1]), "depth" : 3.17 * mm});
        }
    });
